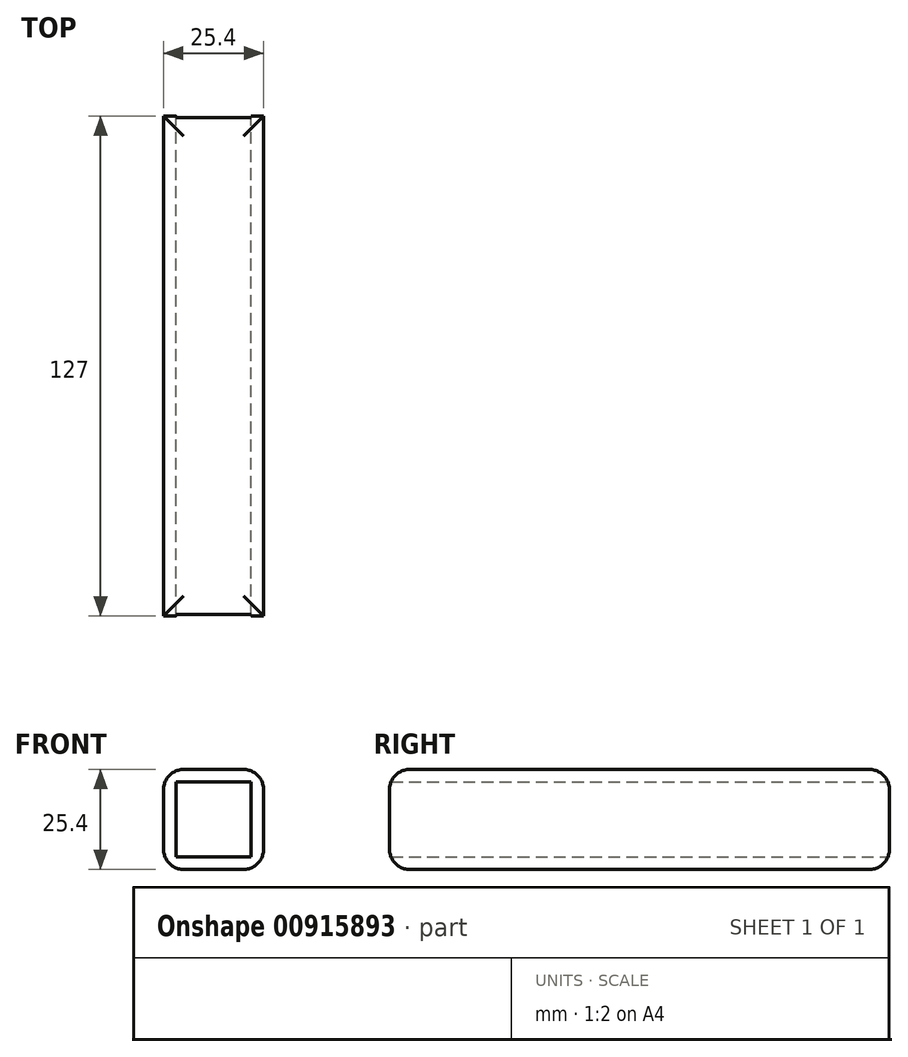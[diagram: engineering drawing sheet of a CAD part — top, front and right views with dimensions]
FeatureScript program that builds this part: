
annotation { "Feature Type Name" : "Feature", "Feature Type Description" : "" }
export const myFeature = defineFeature(function(context is Context, id is Id, definition is map)
    precondition{}
    {
        {
            var Q0;
            Q0=qCreatedBy(makeId("Front.planeOp"),FACE);
            var sketch = newSketch(context, id + "F0", { "sketchPlane" : qUnion([Q0])});
            skLineSegment(sketch, "E0.bottom", {"start": v(-12.7, -12.7) * mm, "end": v(12.7, -12.7) * mm});
            skLineSegment(sketch, "E0.top", {"start": v(-12.7, 12.7) * mm, "end": v(12.7, 12.7) * mm});
            skLineSegment(sketch, "E0.left", {"start": v(-12.7, -12.7) * mm, "end": v(-12.7, 12.7) * mm});
            skLineSegment(sketch, "E0.right", {"start": v(12.7, -12.7) * mm, "end": v(12.7, 12.7) * mm});
            skPoint(sketch, "E0.middle", {"position": v(0, 0) * mm});
            skLineSegment(sketch, "E1.bottom", {"start": v(-9.53, -9.53) * mm, "end": v(9.53, -9.53) * mm});
            skLineSegment(sketch, "E1.top", {"start": v(-9.53, 9.53) * mm, "end": v(9.53, 9.53) * mm});
            skLineSegment(sketch, "E1.left", {"start": v(-9.53, -9.53) * mm, "end": v(-9.53, 9.53) * mm});
            skLineSegment(sketch, "E1.right", {"start": v(9.53, -9.53) * mm, "end": v(9.53, 9.53) * mm});
            skSolve(sketch);
        }
        {
            var Q0;
            Q0=makeQuery(id+"F0.imprint","IMPRINT",FACE,{"disambiguationData":[TD([[makeQuery(id+"F0.imprint","IMPRINT",EDGE,{"derivedFrom":sQuery(id+"F0.wireOp",EDGE,"E0.bottom")}),1.0]])]});
            extrude(context, id + "F1", {"entities" : qUnion([Q0]), "depth" : 127 * mm, "offsetDistance" : 25.4 * mm});
        }
        {
            var Q0;
            Q0=makeQuery(id+"F1.opExtrude","SWEPT_FACE",FACE,{"disambiguationData":[OSD([sQuery(id+"F0.wireOp",EDGE,"E0.top")])]});
            var Q1;
            Q1=makeQuery(id+"F1.opExtrude","SWEPT_FACE",FACE,{"disambiguationData":[OSD([sQuery(id+"F0.wireOp",EDGE,"E0.bottom")])]});
            fillet(context, id + "F2", {"entities" : qUnion([Q0, Q1]), "radius" : 5.08 * mm, "tangentPropagation" : true, "allowEdgeOverflow" : false});
        }
    });
